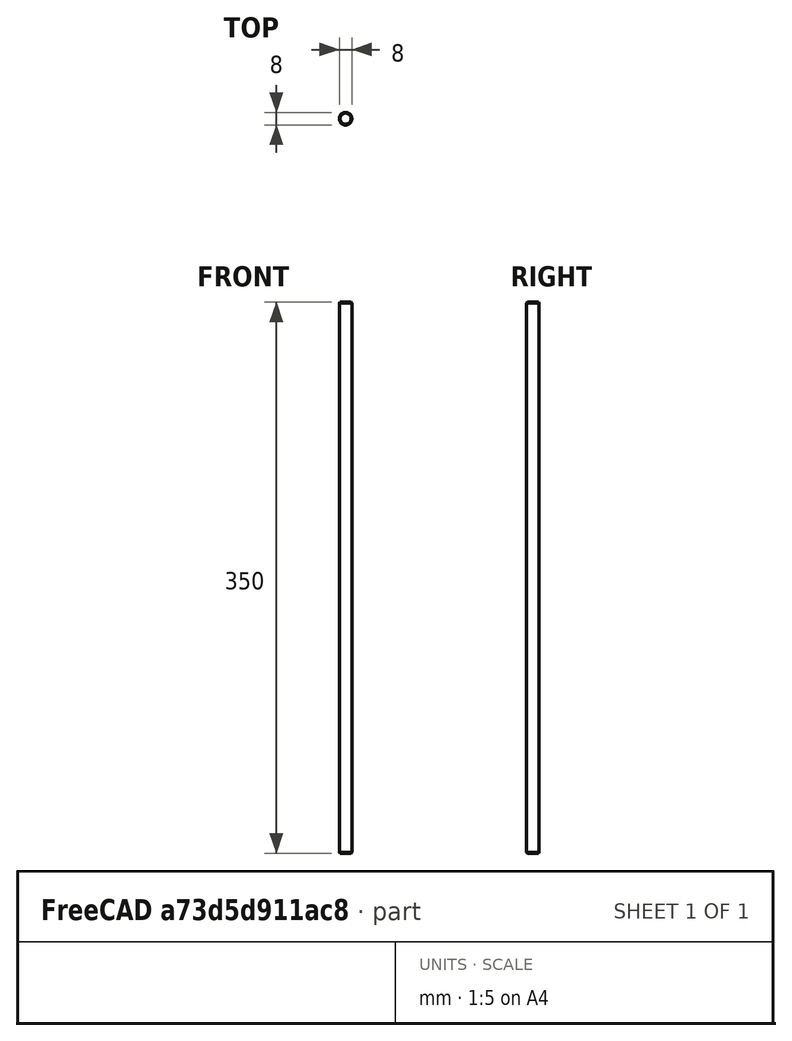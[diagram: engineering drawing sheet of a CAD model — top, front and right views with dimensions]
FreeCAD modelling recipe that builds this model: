
FCSTD DOCUMENT  (FreeCAD 0.21R33771 (Git))
Label: 350mm linear rod
License: All rights reserved
LicenseURL: http://en.wikipedia.org/wiki/All_rights_reserved
objects: Sketcher::SketchObject×1, PartDesign::Pad×1, PartDesign::Chamfer×1, PartDesign::Body×1
note: 6 computed .brp shape members not serialized (recipe doc carries the construction recipe); baked Part::Feature solids carry a one-line shape summary decoded from their .brp

FEATURE [Sketcher::SketchObject] Sketch
  FullyConstrained = true
  MapMode = 5
  Support = -> [XY_Plane]
  sketch-geometry (1):
    g0: Circle CenterX=0 CenterY=0 CenterZ=0 NormalX=0 NormalY=0 NormalZ=1 AngleXU=0 Radius=4
  constraints (2):
    c: Coincident(g0,g-1)
    c: Diameter(g0) = 8
FEATURE [PartDesign::Pad] Pad
  Direction = (0,0,1)
  Length = 350
  Length2 = 10
  Profile = -> Sketch
  ReferenceAxis = -> Sketch [N_Axis]
  Type = 0
FEATURE [PartDesign::Chamfer] Chamfer
  Angle = 45
  Base = -> Pad [Edge2,Edge3]
  BaseFeature = -> Pad
  ChamferType = 0
  FlipDirection = false
  Size = 0.5
  Size2 = 1
  SupportTransform = false
  UseAllEdges = false
FEATURE [PartDesign::Body] Body
  Group = -> [Sketch,Pad,Chamfer]
  Origin = -> Origin
  Tip = -> Chamfer
